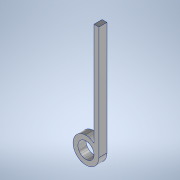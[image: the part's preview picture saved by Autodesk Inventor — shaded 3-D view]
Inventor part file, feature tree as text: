
AUTODESK INVENTOR PART (.ipt)
format: ipt  version: 2022 (Build 260153000, 153)  size: 115,712 bytes
history: native  units: mm
features: extrude x2, sketch x2
ambient origin geometry x8: Origin, YZ Plane, XZ Plane, XY Plane, X Axis, Y Axis, Z Axis, Center Point
bodies: Solid1 (feature_tree)
feature tree (4):
  extrude  "Extrusion1"  Depth=10.0mm
  extrude  "Extrusion2"  TaperAngle=0.0deg  [1 undecoded]
  sketch  "Sketch1"  dims[d0=10.0mm d1=16.0mm]
  sketch  "Sketch2"  dims[d2=5.0mm d3=0.0mm d4=0.0mm d6=5.0mm d7=0.0mm d9=70.0mm d11=3.0mm]
note: 1 required parameter value undecoded (feature->parameter linkage not recoverable at this tier; creation-order binding heuristic only, values carry confidence <= 0.55)
